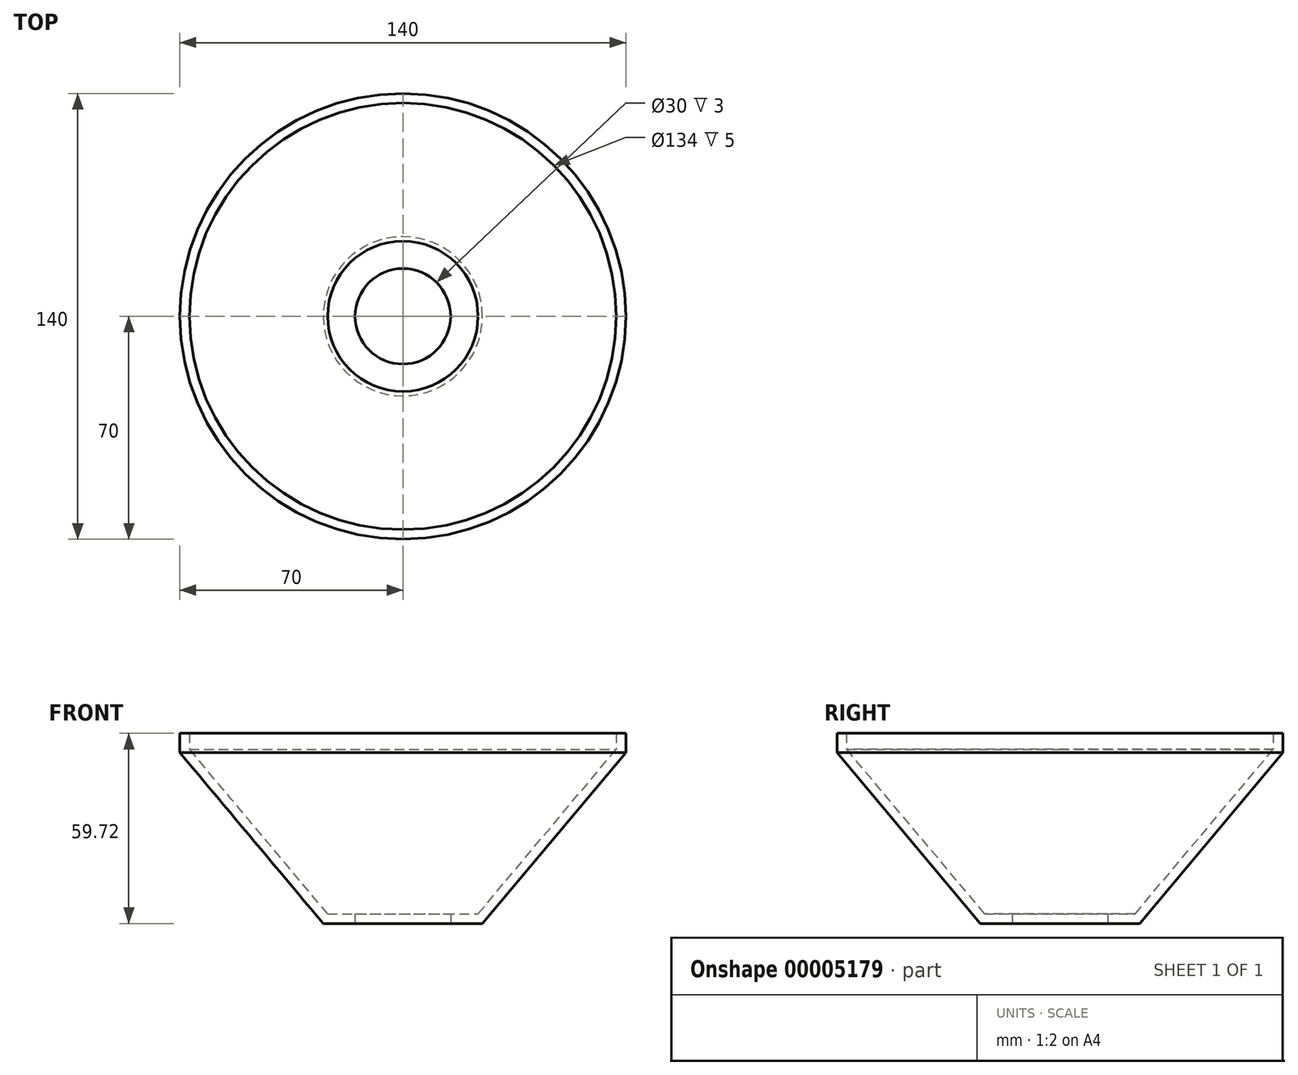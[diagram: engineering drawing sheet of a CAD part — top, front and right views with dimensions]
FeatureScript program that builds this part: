
annotation { "Feature Type Name" : "Feature", "Feature Type Description" : "" }
export const myFeature = defineFeature(function(context is Context, id is Id, definition is map)
    precondition{}
    {
        {
            var Q0;
            Q0=qCreatedBy(makeId("Front.planeOp"),FACE);
            var sketch = newSketch(context, id + "F0", { "sketchPlane" : qUnion([Q0])});
            skLineSegment(sketch, "E0", {"start": v(0, 0) * mm, "end": v(0, 41.46) * mm, "construction": true});
            skLineSegment(sketch, "E1", {"start": v(15, 0) * mm, "end": v(25, 0) * mm});
            skLineSegment(sketch, "E2", {"start": v(25, 0) * mm, "end": v(70, 53.63) * mm});
            skLineSegment(sketch, "E3", {"start": v(70, 53.63) * mm, "end": v(70, 59.72) * mm});
            skLineSegment(sketch, "E4", {"start": v(70, 59.72) * mm, "end": v(67, 59.72) * mm});
            skLineSegment(sketch, "E5", {"start": v(67, 59.72) * mm, "end": v(67, 54.72) * mm});
            skLineSegment(sketch, "E6", {"start": v(67, 54.72) * mm, "end": v(23.6, 3) * mm});
            skLineSegment(sketch, "E7", {"start": v(23.6, 3) * mm, "end": v(15, 3) * mm});
            skLineSegment(sketch, "E8", {"start": v(15, 3) * mm, "end": v(15, 0) * mm});
            skSolve(sketch);
        }
        {
            var Q0;
            Q0 = qSketchRegion(id + "F0", true);
            var Q1;
            Q1=sQuery(id+"F0.wireOp",EDGE,"E0");
            revolve(context, id + "F1", {"entities" : qUnion([Q0]), "axis" : qUnion([Q1]), "revolveType" : RevolveType.FULL});
        }
    });
